# Revit family: Gen_Cultural Room Panel Cladding
name_source: partatom
category: Generic Models
units: mm (PartAtom-declared; Revit-internal decimal feet)

## family parameters
Always vertical = Yes
Can host rebar = No
Cut with Voids When Loaded = Yes
Maintain Annotation Orientation = No
Part Type = Normal
Room Calculation Point = No
Round Connector Dimension = Use Diameter
Shared = No
Work Plane-Based = No

## types (1)
- Gen_Cultural Room Panel Cladding
    Angle = 4.00°
    BasePanelAngle = 4.50°
    Default Elevation = 0 mm  [stored 0 ft]
    Height0 = 750 mm  [stored 2.46063 ft]
    Height1 = 1000 mm  [stored 3.28084 ft]
    Height2 = 1800 mm  [stored 5.90551 ft]
    Height3 = 2400 mm
    Height4 = 3000 mm  [stored 9.84252 ft]
    Material0 = <By Category>
    Material1 = <By Category>
    Material2 = <By Category>
    Material3 = <By Category>
    Material4 = <By Category>
    Panel Number = 40
    PanelHeight = 915 mm  [stored 3.00197 ft]
    RadiusBASE = 3150 mm  [stored 10.3346 ft]

note: [stored X ft] marks values corroborated as IEEE doubles in the binary element streams (Revit-internal decimal feet)

## geometry (parser evidence)
native form markers: Sweep x11
no freeform markers — native parametric forms only
